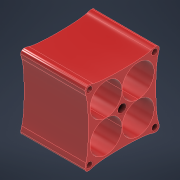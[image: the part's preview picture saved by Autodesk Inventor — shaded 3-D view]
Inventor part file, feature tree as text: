
AUTODESK INVENTOR PART (.ipt)
format: ipt  version: 2022 (Build 260153000, 153)  size: 261,632 bytes
history: native  units: mm
features: extrude x4, sketch x4, fillet x2, projected_geometry x2
ambient origin geometry x8: Origin, YZ Plane, XZ Plane, XY Plane, X Axis, Y Axis, Z Axis, Center Point
bodies: Solid1 (feature_tree)
feature tree (12):
  extrude  "Extrusion1"  Depth=44.0mm
  fillet  "Fillet1"  Radius=38.6mm
  extrude  "Extrusion3"  Depth=3.45mm
  extrude  "Extrusion4"  Depth=3.45mm
  extrude  "Extrusion8"  Depth=2.0mm
  fillet  "Fillet2"  Radius=19.0mm
  sketch  "Sketch1"  dims[d4=44.0mm d5=44.0mm d6=38.6mm]
  sketch  "Sketch3"  dims[d7=3.45mm d8=3.45mm]
  projected_geometry  "Projected Loop3"
  sketch  "Sketch4"  dims[d9=3.45mm d10=3.45mm]
  projected_geometry  "Projected Loop4"
  sketch  "Sketch10"  dims[d11=35.0mm d12=0.0mm d19=2.0mm d24=19.0mm d25=19.0mm d26=19.0mm d27=19.0mm d28=10.0mm d29=10.0mm d30=10.0mm d31=10.0mm d32=3.0mm d33=0.0mm d34=5.0mm d35=38.0mm d36=0.0mm d47=18.0mm d48=2.0mm d49=2.0mm d50=18.0mm d51=2.0mm d52=18.0mm d53=2.0mm d54=18.0mm d55=38.0mm d56=0.0mm d57=10.0mm d58=0.0mm d59=0.0mm d60=0.0mm]
